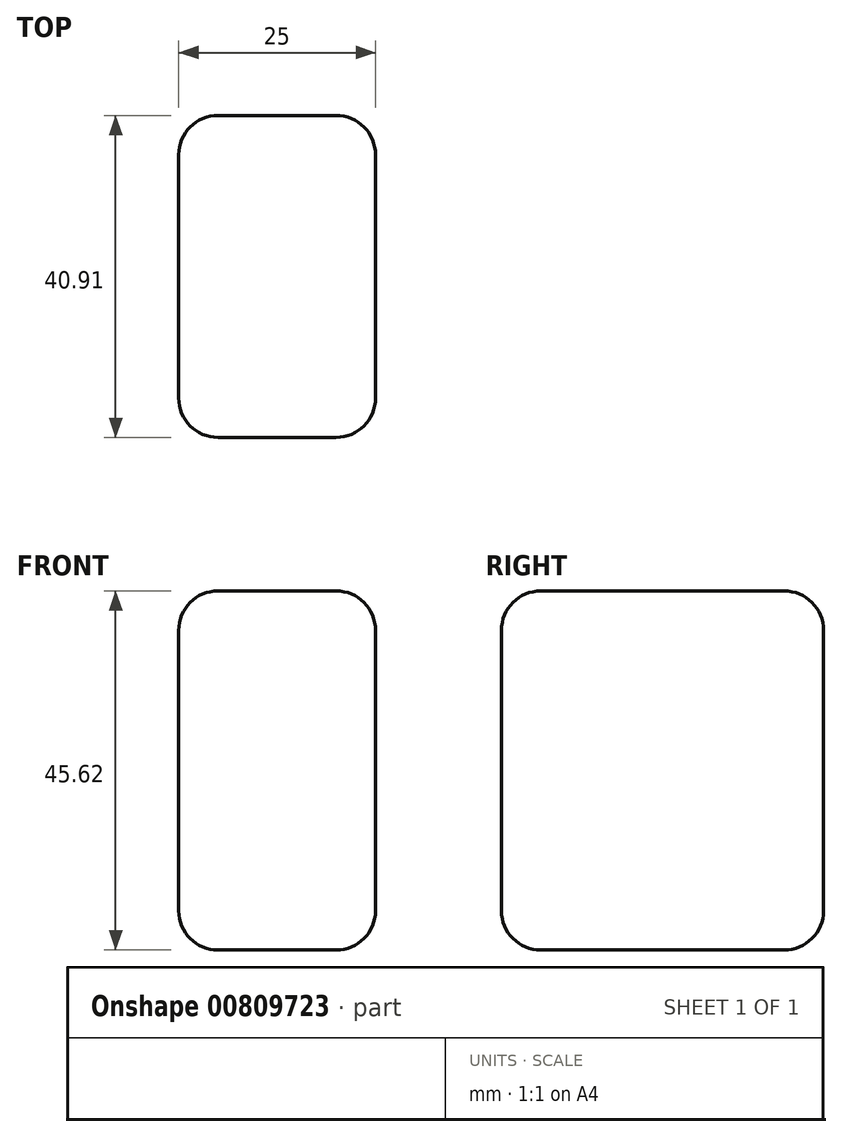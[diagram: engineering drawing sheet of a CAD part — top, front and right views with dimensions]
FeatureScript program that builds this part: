
annotation { "Feature Type Name" : "Feature", "Feature Type Description" : "" }
export const myFeature = defineFeature(function(context is Context, id is Id, definition is map)
    precondition{}
    {
        {
            var Q0;
            Q0=qCreatedBy(makeId("Right.planeOp"),FACE);
            var sketch = newSketch(context, id + "F0", { "sketchPlane" : qUnion([Q0])});
            skLineSegment(sketch, "E0.bottom", {"start": v(-74.25, 56.47) * mm, "end": v(-33.34, 56.47) * mm});
            skLineSegment(sketch, "E0.top", {"start": v(-74.25, 10.85) * mm, "end": v(-33.34, 10.85) * mm});
            skLineSegment(sketch, "E0.left", {"start": v(-74.25, 56.47) * mm, "end": v(-74.25, 10.85) * mm});
            skLineSegment(sketch, "E0.right", {"start": v(-33.34, 56.47) * mm, "end": v(-33.34, 10.85) * mm});
            skSolve(sketch);
        }
        {
            var Q0;
            Q0=makeQuery(id+"F0.imprint","IMPRINT",FACE,{"disambiguationData":[TD([[makeQuery(id+"F0.imprint","IMPRINT",EDGE,{"derivedFrom":sQuery(id+"F0.wireOp",EDGE,"E0.bottom")}),-1.0]])]});
            extrude(context, id + "F1", {"entities" : qUnion([Q0]), "depth" : 25 * mm, "offsetDistance" : 25 * mm});
        }
        {
            var Q0;
            Q0=makeQuery(id+"F1.opExtrude","SWEPT_EDGE",EDGE,{"disambiguationData":[OSD([sQuery(id+"F0.wireOp",EDGE,"E0.bottom"),sQuery(id+"F0.wireOp",EDGE,"E0.right")])]});
            var Q1;
            Q1=makeQuery(id+"F1.opExtrude","CAP_EDGE",EDGE,{"disambiguationData":[OSD([sQuery(id+"F0.wireOp",EDGE,"E0.bottom")])],"isStart":false});
            var Q2;
            Q2=makeQuery(id+"F1.opExtrude","SWEPT_EDGE",EDGE,{"disambiguationData":[OSD([sQuery(id+"F0.wireOp",EDGE,"E0.top"),sQuery(id+"F0.wireOp",EDGE,"E0.left")])]});
            var Q3;
            Q3=makeQuery(id+"F1.opExtrude","CAP_EDGE",EDGE,{"disambiguationData":[OSD([sQuery(id+"F0.wireOp",EDGE,"E0.top")])],"isStart":false});
            var Q4;
            Q4=makeQuery(id+"F1.opExtrude","SWEPT_EDGE",EDGE,{"disambiguationData":[OSD([sQuery(id+"F0.wireOp",EDGE,"E0.bottom"),sQuery(id+"F0.wireOp",EDGE,"E0.left")])]});
            var Q5;
            Q5=makeQuery(id+"F1.opExtrude","CAP_EDGE",EDGE,{"disambiguationData":[OSD([sQuery(id+"F0.wireOp",EDGE,"E0.bottom")])],"isStart":true});
            var Q6;
            Q6=makeQuery(id+"F1.opExtrude","SWEPT_EDGE",EDGE,{"disambiguationData":[OSD([sQuery(id+"F0.wireOp",EDGE,"E0.top"),sQuery(id+"F0.wireOp",EDGE,"E0.right")])]});
            var Q7;
            Q7=makeQuery(id+"F1.opExtrude","CAP_EDGE",EDGE,{"disambiguationData":[OSD([sQuery(id+"F0.wireOp",EDGE,"E0.right")])],"isStart":true});
            var Q8;
            Q8=makeQuery(id+"F1.opExtrude","CAP_EDGE",EDGE,{"disambiguationData":[OSD([sQuery(id+"F0.wireOp",EDGE,"E0.left")])],"isStart":true});
            var Q9;
            Q9=makeQuery(id+"F1.opExtrude","CAP_EDGE",EDGE,{"disambiguationData":[OSD([sQuery(id+"F0.wireOp",EDGE,"E0.left")])],"isStart":false});
            var Q10;
            Q10=makeQuery(id+"F1.opExtrude","CAP_EDGE",EDGE,{"disambiguationData":[OSD([sQuery(id+"F0.wireOp",EDGE,"E0.top")])],"isStart":true});
            var Q11;
            Q11=makeQuery(id+"F1.opExtrude","CAP_EDGE",EDGE,{"disambiguationData":[OSD([sQuery(id+"F0.wireOp",EDGE,"E0.right")])],"isStart":false});
            fillet(context, id + "F2", {"entities" : qUnion([Q0, Q1, Q2, Q3, Q4, Q5, Q6, Q7, Q8, Q9, Q10, Q11]), "radius" : 5 * mm, "tangentPropagation" : true, "allowEdgeOverflow" : false});
        }
    });
